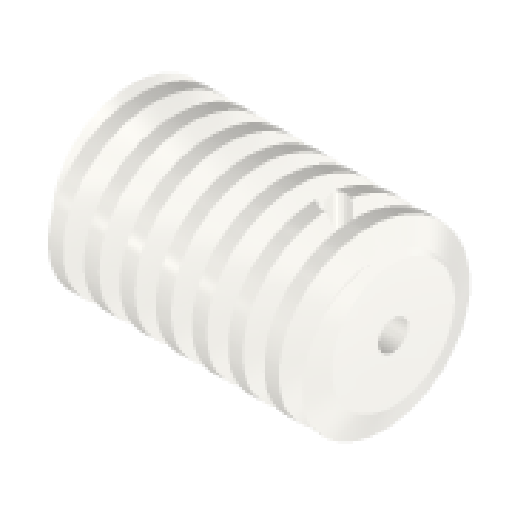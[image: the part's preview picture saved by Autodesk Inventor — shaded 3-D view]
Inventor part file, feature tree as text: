
AUTODESK INVENTOR PART (.ipt)
format: ipt  version: 2024.1 (Build 281209000, 209)  size: 476,672 bytes
history: native  units: mm (DEFAULTED — no unit token found)
features: other x8, extrude x3, chamfer x2, pattern_circular x2, sketch x2, reference x1
ambient origin geometry x6: Origin, XZ Plane, X Axis, Y Axis, Z Axis, Center Point
bodies: Solid1 (feature_tree)
feature tree (18):
  extrude  "Grundkörper"  Depth=19.0mm
  chamfer  "Chamfer1"  [1 undecoded]
  chamfer  "Chamfer2"  Distance=1.000918mm
  other  "Zahnskizze"
  other  "Zahn"
  pattern_circular  "Zahnanordnung"  [2 undecoded]
  other  "Linker Zahn"
  pattern_circular  "Linke Zahnanordnung"  [2 undecoded]
  extrude  "Extrusion2"  Depth=10.0mm
  extrude  "Extrusion3"  Depth=10.0mm
  other  "Grundkörperskizze"
  other  "Srf1"
  sketch  "Skizze6"  dims[d4=40.0mm d5=19.0mm]
  reference  "Referenz1"
  sketch  "Skizze7"  dims[d6=30.0mm d7=0.0mm d8=1.000918mm d9=2.75mm d10=1.000918mm d11=2.75mm d12=19.198622mm d14=3.1425mm d24=19.198622mm d25=21.20575mm d26=0.981748mm d27=7.0mm d28=9.0mm d29=10.7mm d30=22.5deg d31=10.0mm d32=100.0mm d33=0.0mm d34=90.0deg d35=90.0deg d36=0.0mm d37=0.0mm d44=10.0mm d46=360.0deg d47=45.0deg d48=45.0deg d49=28.975mm d50=0.0mm d54=0.0mm d56=0.0mm d59=18.75mm d60=10.0mm d61=0.0mm d62=22.5deg d63=10.0mm d64=150.0mm d65=0.0mm d66=90.0deg d67=90.0deg d68=0.0mm d69=0.0mm d70=10.0mm d71=10.0mm d72=10.0mm d73=360.0deg d75=10.0mm d76=10.0mm d77=0.0mm d79=28.975mm d80=0.0mm d81=0.0mm d82=0.089012mm d83=2.8mm d84=0.0mm d85=0.0mm d86=2.7mm]
  other  "Flankendurchmesser"
  other  "Assembly_Planktoscope_Uc2version_wormdrive_V3.iam"
  other  "00_NEMA11:1"
note: 5 required parameter values undecoded (feature->parameter linkage not recoverable at this tier; creation-order binding heuristic only, values carry confidence <= 0.55)
